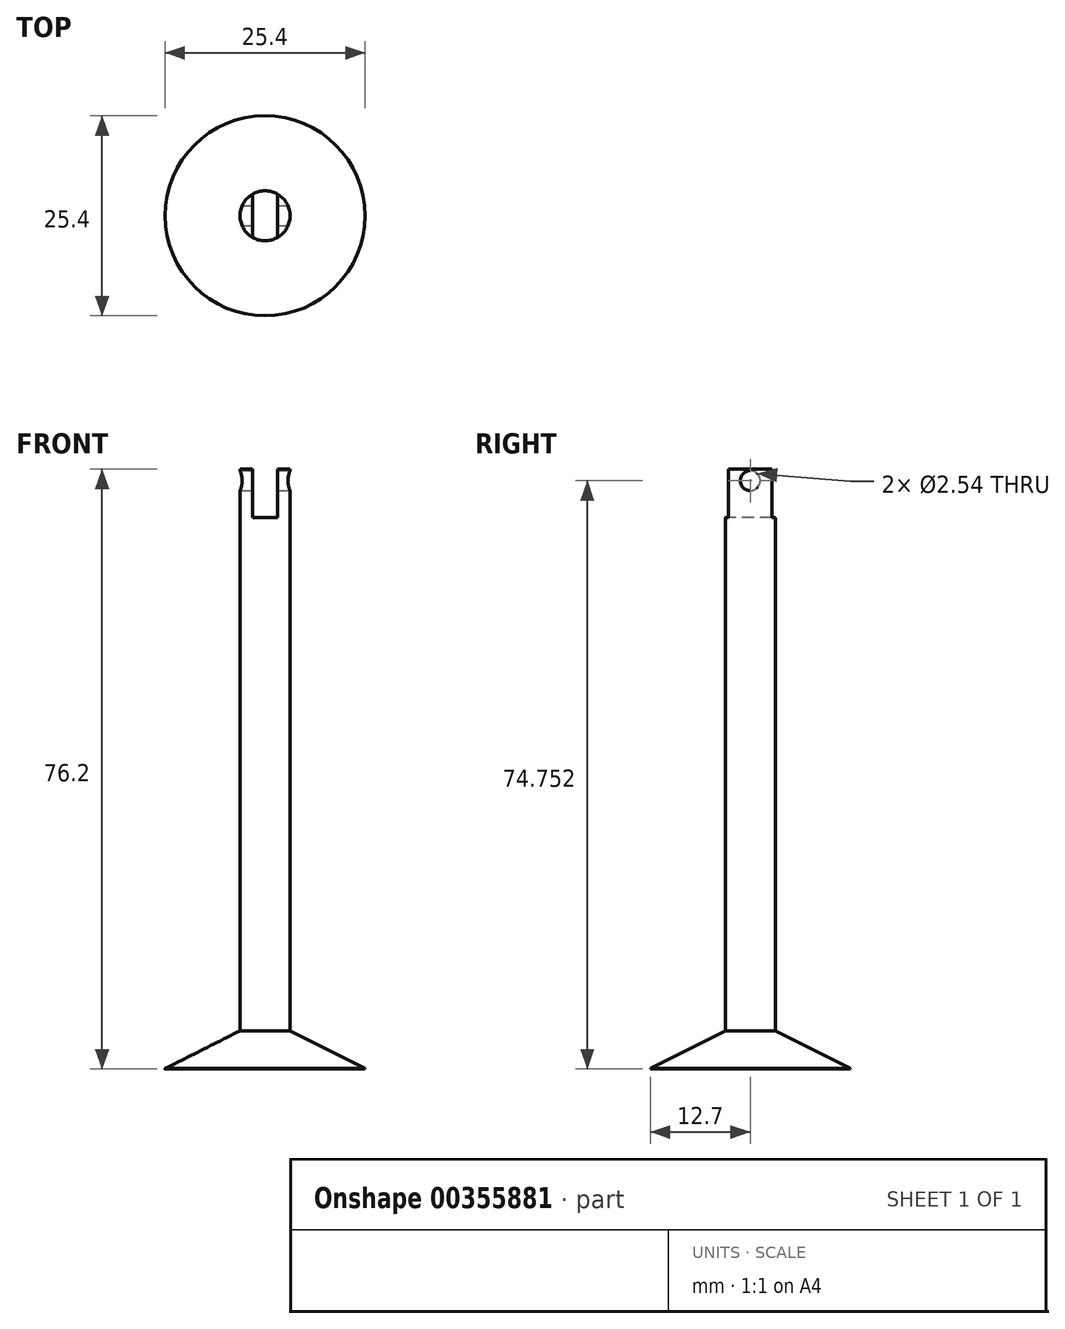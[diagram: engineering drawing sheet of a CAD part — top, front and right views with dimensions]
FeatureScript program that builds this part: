
annotation { "Feature Type Name" : "Feature", "Feature Type Description" : "" }
export const myFeature = defineFeature(function(context is Context, id is Id, definition is map)
    precondition{}
    {
        {
            var Q0;
            Q0=qCreatedBy(makeId("Top.planeOp"),FACE);
            var sketch = newSketch(context, id + "F0", { "sketchPlane" : qUnion([Q0])});
            skCircle(sketch, "E0", {"center": v(0, 0) * mm, "radius": 12.7 * mm});
            skSolve(sketch);
        }
        {
            var Q0;
            Q0=qSketchRegion(id+"F0",true);
            extrude(context, id + "F1", {"entities" : qUnion([Q0]), "depth" : 76.2 * mm});
        }
        {
            var Q0;
            Q0=qCreatedBy(makeId("Front.planeOp"),FACE);
            var sketch = newSketch(context, id + "F2", { "sketchPlane" : qUnion([Q0])});
            skLineSegment(sketch, "E1.bottom", {"start": v(3.17, 0) * mm, "end": v(-3.18, 0) * mm});
            skLineSegment(sketch, "E1.top", {"start": v(3.17, 153.74) * mm, "end": v(-3.18, 153.74) * mm});
            skLineSegment(sketch, "E1.left", {"start": v(3.17, 0) * mm, "end": v(3.17, 153.74) * mm});
            skLineSegment(sketch, "E1.right", {"start": v(-3.18, 0) * mm, "end": v(-3.18, 153.74) * mm});
            skPoint(sketch, "E1.middle", {"position": v(0, 76.87) * mm});
            skLineSegment(sketch, "E2", {"start": v(-3.18, 4.87) * mm, "end": v(-17.21, -2.22) * mm});
            skLineSegment(sketch, "E3", {"start": v(-17.21, -2.22) * mm, "end": v(-17.21, 83.75) * mm});
            skLineSegment(sketch, "E4", {"start": v(-17.21, 83.75) * mm, "end": v(-3.18, 83.75) * mm});
            skSolve(sketch);
        }
        {
            var Q0;
            {var subQ0=sQuery(id+"F2.wireOp",EDGE,"E2");Q0=makeQuery(id+"F2.imprint","IMPRINT",FACE,{"disambiguationData":[TD([[makeQuery(id+"F2.imprint","IMPRINT",EDGE,{"derivedFrom":subQ0}),-1.0]])]});}
            var Q1;
            Q1=makeQuery(id+"F1.opExtrude","CAP_EDGE",EDGE,{"disambiguationData":[OSD([sQuery(id+"F0.wireOp",EDGE,"E0")])],"isStart":false});
            revolve(context, id + "F3", {"operationType" : NewBodyOperationType.REMOVE, "entities" : qUnion([Q0]), "axis" : qUnion([Q1]), "revolveType" : RevolveType.FULL, "oppositeDirection" : true});
        }
        {
            var Q0;
            Q0=qCreatedBy(makeId("Front.planeOp"),FACE);
            var sketch = newSketch(context, id + "F4", { "sketchPlane" : qUnion([Q0])});
            skLineSegment(sketch, "E5.bottom", {"start": v(1.59, 70.06) * mm, "end": v(-1.59, 70.06) * mm});
            skLineSegment(sketch, "E5.top", {"start": v(1.59, 82.76) * mm, "end": v(-1.59, 82.76) * mm});
            skLineSegment(sketch, "E5.left", {"start": v(1.59, 70.06) * mm, "end": v(1.59, 82.76) * mm});
            skLineSegment(sketch, "E5.right", {"start": v(-1.59, 70.06) * mm, "end": v(-1.59, 82.76) * mm});
            skPoint(sketch, "E5.middle", {"position": v(0, 76.4) * mm});
            skSolve(sketch);
        }
        {
            var Q0;
            Q0=makeQuery(id+"F4.imprint","IMPRINT",FACE,{"disambiguationData":[TD([[makeQuery(id+"F4.imprint","IMPRINT",EDGE,{"derivedFrom":sQuery(id+"F4.wireOp",EDGE,"E5.bottom")}),-1.0]])]});
            extrude(context, id + "F5", {"entities" : qUnion([Q0]), "operationType" : NewBodyOperationType.REMOVE, "endBound" : BoundingType.SYMMETRIC, "oppositeDirection" : true, "depth" : 25.4 * mm});
        }
        {
            var Q0;
            Q0=qCreatedBy(makeId("Right.planeOp"),FACE);
            var sketch = newSketch(context, id + "F6", { "sketchPlane" : qUnion([Q0])});
            skCircle(sketch, "E6", {"center": v(0, 74.75) * mm, "radius": 4.45 * mm});
            skCircle(sketch, "E7", {"center": v(0, 74.75) * mm, "radius": 1.27 * mm});
            skSolve(sketch);
        }
        {
            var Q0;
            Q0=makeQuery(id+"F6.imprint","IMPRINT",FACE,{"disambiguationData":[TD([[makeQuery(id+"F6.imprint","IMPRINT",EDGE,{"derivedFrom":sQuery(id+"F6.wireOp",EDGE,"E7")}),1.0]])]});
            extrude(context, id + "F7", {"entities" : qUnion([Q0]), "operationType" : NewBodyOperationType.REMOVE, "endBound" : BoundingType.SYMMETRIC, "oppositeDirection" : true, "depth" : 25.4 * mm});
        }
    });
